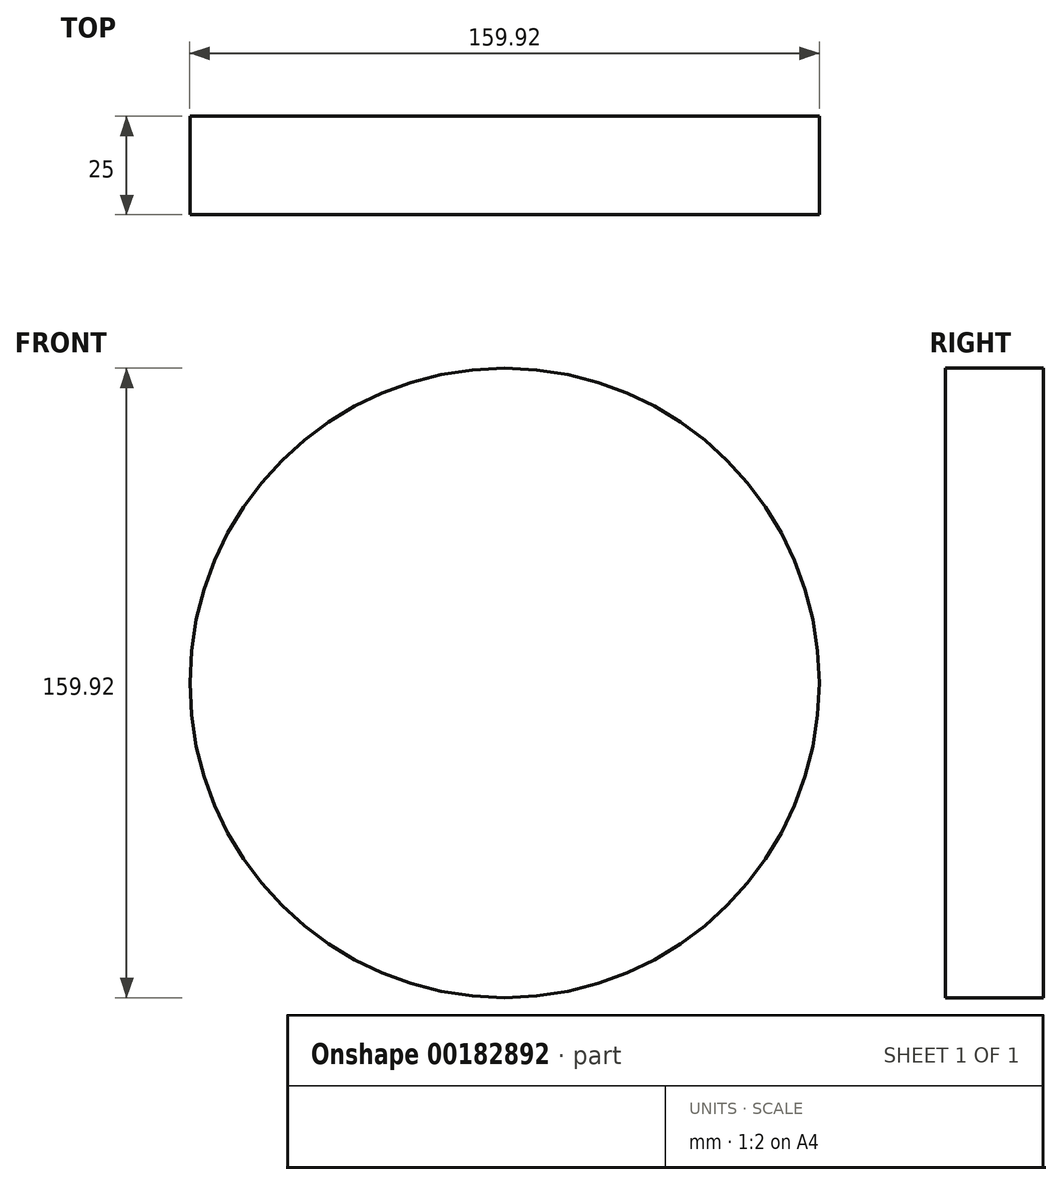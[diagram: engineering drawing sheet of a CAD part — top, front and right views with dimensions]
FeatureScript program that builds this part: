
annotation { "Feature Type Name" : "Feature", "Feature Type Description" : "" }
export const myFeature = defineFeature(function(context is Context, id is Id, definition is map)
    precondition{}
    {
        {
            var Q0;
            Q0=qCreatedBy(makeId("Front.planeOp"),FACE);
            var sketch = newSketch(context, id + "F0", { "sketchPlane" : qUnion([Q0])});
            skCircle(sketch, "E0", {"center": v(0, 0) * mm, "radius": 79.96 * mm});
            skSolve(sketch);
        }
        {
            var Q0;
            Q0=makeQuery(id+"F0.imprint","IMPRINT",FACE,{"disambiguationData":[TD([[makeQuery(id+"F0.imprint","IMPRINT",EDGE,{"derivedFrom":sQuery(id+"F0.wireOp",EDGE,"E0")}),1.0]])]});
            extrude(context, id + "F1", {"entities" : qUnion([Q0]), "depth" : 25 * mm});
        }
    });
